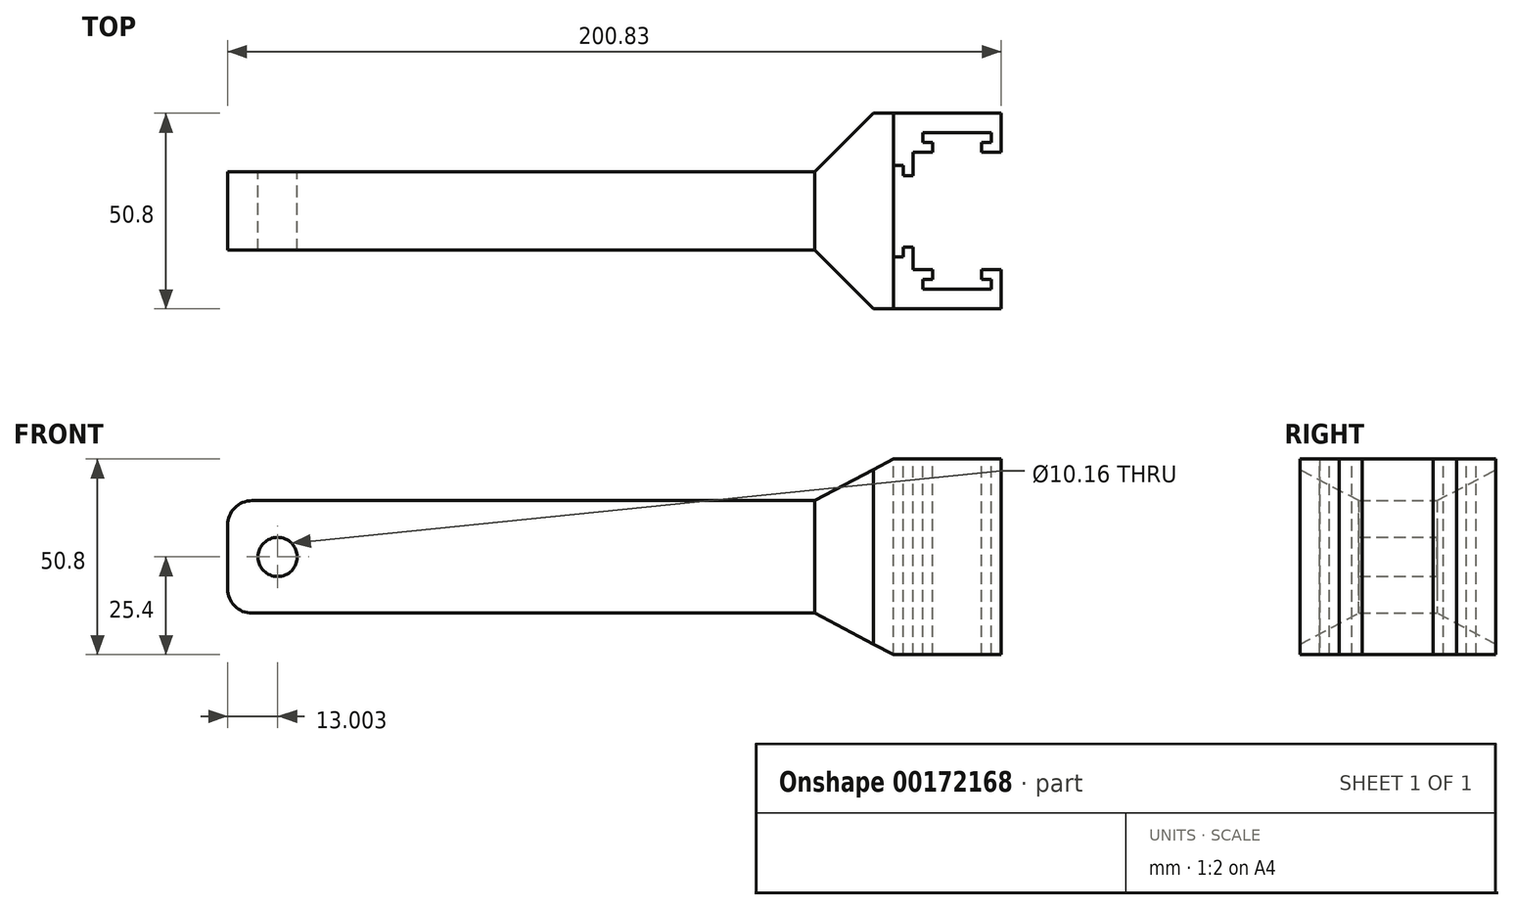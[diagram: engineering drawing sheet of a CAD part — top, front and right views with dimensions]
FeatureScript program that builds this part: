
annotation { "Feature Type Name" : "Feature", "Feature Type Description" : "" }
export const myFeature = defineFeature(function(context is Context, id is Id, definition is map)
    precondition{}
    {
        {
            var Q0;
            Q0=qCreatedBy(makeId("Front.planeOp"),FACE);
            var sketch = newSketch(context, id + "F0", { "sketchPlane" : qUnion([Q0])});
            skLineSegment(sketch, "E0.bottom", {"start": v(76.2, 14.6) * mm, "end": v(-69.85, 14.6) * mm});
            skLineSegment(sketch, "E0.top", {"start": v(76.2, -14.6) * mm, "end": v(-69.85, -14.6) * mm});
            skLineSegment(sketch, "E0.left", {"start": v(76.2, 14.6) * mm, "end": v(76.2, -14.6) * mm});
            skLineSegment(sketch, "E0.right", {"start": v(-76.2, 8.26) * mm, "end": v(-76.2, -8.26) * mm});
            skPoint(sketch, "E0.middle", {"position": v(0, 0) * mm});
            skLineSegment(sketch, "E1.bottom", {"start": v(96.7, 25.4) * mm, "end": v(124.63, 25.4) * mm});
            skLineSegment(sketch, "E1.top", {"start": v(96.7, -25.4) * mm, "end": v(124.63, -25.4) * mm});
            skLineSegment(sketch, "E1.left", {"start": v(96.7, 25.4) * mm, "end": v(96.7, -25.4) * mm});
            skLineSegment(sketch, "E1.right", {"start": v(124.63, 25.4) * mm, "end": v(124.63, -25.4) * mm});
            skPoint(sketch, "E1.middle", {"position": v(110.66, 0) * mm});
            skLineSegment(sketch, "E2", {"start": v(76.2, 14.6) * mm, "end": v(96.7, 25.4) * mm});
            skLineSegment(sketch, "E3", {"start": v(76.2, -14.6) * mm, "end": v(96.7, -25.4) * mm});
            skPoint(sketch, "E4.visualSharp", {"position": v(-76.2, 14.6) * mm});
            skArc(sketch, "E4.filletArc", {"start": v(-69.85, 14.6) * mm, "mid": v(-74.34, 12.75) * mm, "end": v(-76.2, 8.26) * mm});
            skPoint(sketch, "E5.visualSharp", {"position": v(-76.2, -14.6) * mm});
            skArc(sketch, "E5.filletArc", {"start": v(-76.2, -8.26) * mm, "mid": v(-74.34, -12.75) * mm, "end": v(-69.85, -14.6) * mm});
            skCircle(sketch, "E6", {"center": v(-63.2, 0) * mm, "radius": 5.08 * mm});
            skLineSegment(sketch, "E7", {"start": v(101.77, 25.4) * mm, "end": v(101.77, -25.4) * mm});
            skLineSegment(sketch, "E8", {"start": v(119.55, 25.4) * mm, "end": v(119.55, -25.4) * mm});
            skSolve(sketch);
        }
        {
            var Q0;
            Q0=makeQuery(id+"F0.imprint","IMPRINT",FACE,{"disambiguationData":[TD([[makeQuery(id+"F0.imprint","IMPRINT",EDGE,{"derivedFrom":sQuery(id+"F0.wireOp",EDGE,"E0.bottom")}),1.0]])]});
            extrude(context, id + "F1", {"entities" : qUnion([Q0]), "endBound" : BoundingType.SYMMETRIC, "depth" : 20.32 * mm});
        }
        {
            var Q0;
            {var subQ0=sQuery(id+"F0.wireOp",EDGE,"E1.right");Q0=makeQuery(id+"F0.imprint","IMPRINT",FACE,{"disambiguationData":[TD([[makeQuery(id+"F0.imprint","IMPRINT",EDGE,{"derivedFrom":subQ0}),-1.0]])]});}
            var Q1;
            {var subQ0=sQuery(id+"F0.wireOp",EDGE,"E7");Q1=makeQuery(id+"F0.imprint","IMPRINT",FACE,{"disambiguationData":[TD([[makeQuery(id+"F0.imprint","IMPRINT",EDGE,{"derivedFrom":subQ0}),1.0]])]});}
            var Q2;
            {var subQ0=sQuery(id+"F0.wireOp",EDGE,"E1.left");Q2=makeQuery(id+"F0.imprint","IMPRINT",FACE,{"disambiguationData":[TD([[makeQuery(id+"F0.imprint","IMPRINT",EDGE,{"derivedFrom":subQ0}),1.0]])]});}
            var Q3;
            Q3=makeQuery(id+"F0.imprint","IMPRINT",FACE,{"disambiguationData":[TD([[makeQuery(id+"F0.imprint","IMPRINT",EDGE,{"derivedFrom":sQuery(id+"F0.wireOp",EDGE,"E0.left")}),1.0]])]});
            extrude(context, id + "F2", {"entities" : qUnion([Q0, Q1, Q2, Q3]), "endBound" : BoundingType.SYMMETRIC, "depth" : 50.8 * mm});
        }
        {
            var Q0;
            Q0=makeQuery(id+"F2.opExtrude","CAP_EDGE",EDGE,{"disambiguationData":[OSD([sQuery(id+"F0.wireOp",EDGE,"E0.left")])],"isStart":false});
            var Q1;
            Q1=makeQuery(id+"F2.opExtrude","CAP_EDGE",EDGE,{"disambiguationData":[OSD([sQuery(id+"F0.wireOp",EDGE,"E0.left")])],"isStart":true});
            chamfer(context, id + "F3", {"entities" : qUnion([Q0, Q1]), "width" : 15.24 * mm, "tangentPropagation" : true});
        }
        {
            var Q0;
            Q0=makeQuery(id+"F2.opExtrude","SWEPT_FACE",FACE,{"disambiguationData":[OSD([sQuery(id+"F0.wireOp",EDGE,"E1.bottom")])]});
            var sketch = newSketch(context, id + "F4", { "sketchPlane" : qUnion([Q0])});
            skLineSegment(sketch, "E9.bottom", {"start": v(124.63, 12.7) * mm, "end": v(101.77, 12.7) * mm});
            skLineSegment(sketch, "E9.top", {"start": v(124.63, -12.7) * mm, "end": v(101.77, -12.7) * mm});
            skLineSegment(sketch, "E9.left", {"start": v(124.63, 12.7) * mm, "end": v(124.63, -12.7) * mm});
            skLineSegment(sketch, "E9.right", {"start": v(101.77, 12.7) * mm, "end": v(101.77, -12.7) * mm});
            skLineSegment(sketch, "E10.bottom", {"start": v(106.85, -20.32) * mm, "end": v(119.55, -20.32) * mm});
            skLineSegment(sketch, "E10.top", {"start": v(106.85, 20.32) * mm, "end": v(119.55, 20.32) * mm});
            skLineSegment(sketch, "E10.left", {"start": v(106.85, -20.32) * mm, "end": v(106.85, 20.32) * mm});
            skLineSegment(sketch, "E10.right", {"start": v(119.55, -20.32) * mm, "end": v(119.55, 20.32) * mm});
            skPoint(sketch, "E10.middle", {"position": v(113.2, 0) * mm});
            skLineSegment(sketch, "E11.bottom", {"start": v(101.77, -15.24) * mm, "end": v(147.5, -15.24) * mm});
            skLineSegment(sketch, "E11.top", {"start": v(101.77, 15.24) * mm, "end": v(147.5, 15.24) * mm});
            skLineSegment(sketch, "E11.left", {"start": v(101.77, -15.24) * mm, "end": v(101.77, 15.24) * mm});
            skLineSegment(sketch, "E11.right", {"start": v(147.5, -15.24) * mm, "end": v(147.5, 15.24) * mm});
            skPoint(sketch, "E11.middle", {"position": v(124.63, 0) * mm});
            skSolve(sketch);
        }
        {
            var Q0;
            Q0=makeQuery(id+"F4.imprint","IMPRINT",FACE,{"disambiguationData":[TD([[makeQuery(id+"F4.imprint","IMPRINT",EDGE,{"derivedFrom":sQuery(id+"F4.wireOp",EDGE,"E9.bottom")}),1.0]])]});
            extrude(context, id + "F5", {"entities" : qUnion([Q0]), "operationType" : NewBodyOperationType.REMOVE, "oppositeDirection" : true, "depth" : 64.77 * mm});
        }
        {
            var Q0;
            {var subQ0=sQuery(id+"F4.wireOp",EDGE,"E10.right");var subQ1=sQuery(id+"F4.wireOp",EDGE,"E9.bottom");var subQ2=makeQuery(id+"F4.imprint","INTERSECT",VERTEX,{"derivedFrom":[subQ1,subQ0]});Q0=makeQuery(id+"F4.imprint","IMPRINT",FACE,{"disambiguationData":[TD([[makeQuery(id+"F4.imprint","IMPRINT",EDGE,{"disambiguationData":[TD([[subQ2,-1.0]])],"derivedFrom":subQ1}),-1.0]])]});}
            var Q1;
            {var subQ0=sQuery(id+"F4.wireOp",EDGE,"E10.top");Q1=makeQuery(id+"F4.imprint","IMPRINT",FACE,{"disambiguationData":[TD([[makeQuery(id+"F4.imprint","IMPRINT",EDGE,{"derivedFrom":subQ0}),-1.0]])]});}
            var Q2;
            {var subQ0=sQuery(id+"F4.wireOp",EDGE,"E10.right");var subQ1=sQuery(id+"F4.wireOp",EDGE,"E9.top");var subQ2=makeQuery(id+"F4.imprint","INTERSECT",VERTEX,{"derivedFrom":[subQ1,subQ0]});Q2=makeQuery(id+"F4.imprint","IMPRINT",FACE,{"disambiguationData":[TD([[makeQuery(id+"F4.imprint","IMPRINT",EDGE,{"disambiguationData":[TD([[subQ2,-1.0]])],"derivedFrom":subQ1}),1.0]])]});}
            var Q3;
            {var subQ0=sQuery(id+"F4.wireOp",EDGE,"E10.bottom");Q3=makeQuery(id+"F4.imprint","IMPRINT",FACE,{"disambiguationData":[TD([[makeQuery(id+"F4.imprint","IMPRINT",EDGE,{"derivedFrom":subQ0}),1.0]])]});}
            var Q4;
            {var subQ0=sQuery(id+"F4.wireOp",EDGE,"E11.left");var subQ1=sQuery(id+"F4.wireOp",EDGE,"E9.bottom");var subQ2=makeQuery(id+"F4.imprint","INTERSECT",VERTEX,{"derivedFrom":[subQ1,subQ0]});Q4=makeQuery(id+"F4.imprint","IMPRINT",FACE,{"disambiguationData":[TD([[makeQuery(id+"F4.imprint","IMPRINT",EDGE,{"disambiguationData":[TD([[subQ2,1.0]])],"derivedFrom":subQ1}),-1.0]])]});}
            var Q5;
            {var subQ0=sQuery(id+"F4.wireOp",EDGE,"E9.bottom");var subQ3=sQuery(id+"F4.wireOp",EDGE,"E10.right");var subQ4=makeQuery(id+"F4.imprint","INTERSECT",VERTEX,{"derivedFrom":[subQ0,subQ3]});Q5=makeQuery(id+"F4.imprint","IMPRINT",FACE,{"disambiguationData":[TD([[makeQuery(id+"F4.imprint","IMPRINT",EDGE,{"disambiguationData":[TD([[subQ4,-1.0]])],"derivedFrom":subQ3}),-1.0]])]});}
            var Q6;
            {var subQ0=sQuery(id+"F4.wireOp",EDGE,"E9.top");var subQ3=sQuery(id+"F4.wireOp",EDGE,"E10.right");var subQ4=makeQuery(id+"F4.imprint","INTERSECT",VERTEX,{"derivedFrom":[subQ0,subQ3]});Q6=makeQuery(id+"F4.imprint","IMPRINT",FACE,{"disambiguationData":[TD([[makeQuery(id+"F4.imprint","IMPRINT",EDGE,{"disambiguationData":[TD([[subQ4,1.0]])],"derivedFrom":subQ3}),-1.0]])]});}
            var Q7;
            {var subQ0=sQuery(id+"F4.wireOp",EDGE,"E11.left");var subQ1=sQuery(id+"F4.wireOp",EDGE,"E9.top");var subQ2=makeQuery(id+"F4.imprint","INTERSECT",VERTEX,{"derivedFrom":[subQ1,subQ0]});Q7=makeQuery(id+"F4.imprint","IMPRINT",FACE,{"disambiguationData":[TD([[makeQuery(id+"F4.imprint","IMPRINT",EDGE,{"disambiguationData":[TD([[subQ2,1.0]])],"derivedFrom":subQ1}),1.0]])]});}
            extrude(context, id + "F6", {"entities" : qUnion([Q0, Q1, Q2, Q3, Q4, Q5, Q6, Q7]), "operationType" : NewBodyOperationType.REMOVE, "endBound" : BoundingType.SYMMETRIC, "oppositeDirection" : true, "depth" : 159 * mm});
        }
        {
            var Q0;
            {var subQ15=sQuery(id+"F4.wireOp",EDGE,"E10.bottom");Q0=makeQuery(id+"F4.imprint","IMPRINT",FACE,{"disambiguationData":[TD([[makeQuery(id+"F4.imprint","IMPRINT",EDGE,{"derivedFrom":subQ15}),-1.0]])]});}
            var sketch = newSketch(context, id + "F7", { "sketchPlane" : qUnion([Q0])});
            skLineSegment(sketch, "E12.bottom", {"start": v(122.1, 20.33) * mm, "end": v(104.31, 20.33) * mm});
            skLineSegment(sketch, "E12.top", {"start": v(122.1, 17.78) * mm, "end": v(104.31, 17.78) * mm});
            skLineSegment(sketch, "E12.left", {"start": v(122.1, 20.33) * mm, "end": v(122.1, 17.78) * mm});
            skLineSegment(sketch, "E12.right", {"start": v(104.31, 20.33) * mm, "end": v(104.31, 17.78) * mm});
            skLineSegment(sketch, "E13.bottom", {"start": v(104.31, 17.78) * mm, "end": v(122.1, 17.78) * mm, "construction": true});
            skLineSegment(sketch, "E13.top", {"start": v(104.31, -17.78) * mm, "end": v(122.1, -17.78) * mm, "construction": true});
            skLineSegment(sketch, "E13.left", {"start": v(104.31, 17.78) * mm, "end": v(104.31, -17.78) * mm, "construction": true});
            skLineSegment(sketch, "E13.right", {"start": v(122.1, 17.78) * mm, "end": v(122.1, -17.78) * mm, "construction": true});
            skLineSegment(sketch, "E14.bottom", {"start": v(104.31, -17.78) * mm, "end": v(122.1, -17.78) * mm});
            skLineSegment(sketch, "E14.top", {"start": v(104.31, -20.31) * mm, "end": v(122.1, -20.31) * mm});
            skLineSegment(sketch, "E14.left", {"start": v(104.31, -17.78) * mm, "end": v(104.31, -20.31) * mm});
            skLineSegment(sketch, "E14.right", {"start": v(122.1, -17.78) * mm, "end": v(122.1, -20.31) * mm});
            skSolve(sketch);
        }
        {
            var Q0;
            Q0=makeQuery(id+"F7.imprint","IMPRINT",FACE,{"disambiguationData":[TD([[makeQuery(id+"F7.imprint","IMPRINT",EDGE,{"derivedFrom":sQuery(id+"F7.wireOp",EDGE,"E12.bottom")}),1.0]])]});
            extrude(context, id + "F8", {"entities" : qUnion([Q0]), "operationType" : NewBodyOperationType.REMOVE, "oppositeDirection" : true, "depth" : 59.44 * mm});
        }
        {
            var Q0;
            {var subQ0=sQuery(id+"F7.wireOp",EDGE,"E14.left");Q0=makeQuery(id+"F7.imprint","IMPRINT",FACE,{"disambiguationData":[TD([[makeQuery(id+"F7.imprint","IMPRINT",EDGE,{"derivedFrom":subQ0}),1.0]])]});}
            var Q1;
            {var subQ0=sQuery(id+"F7.wireOp",EDGE,"E14.right");Q1=makeQuery(id+"F7.imprint","IMPRINT",FACE,{"disambiguationData":[TD([[makeQuery(id+"F7.imprint","IMPRINT",EDGE,{"derivedFrom":subQ0}),-1.0]])]});}
            extrude(context, id + "F9", {"entities" : qUnion([Q0, Q1]), "operationType" : NewBodyOperationType.REMOVE, "oppositeDirection" : true, "depth" : 72.9 * mm});
        }
        {
            var Q0;
            {var subQ15=sQuery(id+"F4.wireOp",EDGE,"E10.bottom");Q0=makeQuery(id+"F4.imprint","IMPRINT",FACE,{"disambiguationData":[TD([[makeQuery(id+"F4.imprint","IMPRINT",EDGE,{"derivedFrom":subQ15}),-1.0]])]});}
            var sketch = newSketch(context, id + "F10", { "sketchPlane" : qUnion([Q0])});
            skLineSegment(sketch, "E15.bottom", {"start": v(101.77, 11.8) * mm, "end": v(96.7, 11.8) * mm});
            skLineSegment(sketch, "E15.top", {"start": v(101.77, -11.94) * mm, "end": v(96.7, -11.94) * mm});
            skLineSegment(sketch, "E15.left", {"start": v(101.77, 11.8) * mm, "end": v(101.77, -11.94) * mm});
            skLineSegment(sketch, "E15.right", {"start": v(96.7, 11.8) * mm, "end": v(96.7, -11.94) * mm});
            skLineSegment(sketch, "E16.bottom", {"start": v(101.77, 11.8) * mm, "end": v(99.23, 11.8) * mm});
            skLineSegment(sketch, "E16.top", {"start": v(101.77, -11.94) * mm, "end": v(99.23, -11.94) * mm});
            skLineSegment(sketch, "E16.right", {"start": v(99.23, 11.8) * mm, "end": v(99.23, -11.94) * mm});
            skLineSegment(sketch, "E17", {"start": v(101.77, -9.3) * mm, "end": v(99.23, -9.3) * mm});
            skLineSegment(sketch, "E18", {"start": v(101.77, 9.17) * mm, "end": v(99.23, 9.17) * mm});
            skSolve(sketch);
        }
        {
            var Q0;
            {var subQ0=sQuery(id+"F10.wireOp",EDGE,"E17");Q0=makeQuery(id+"F10.imprint","IMPRINT",FACE,{"disambiguationData":[TD([[makeQuery(id+"F10.imprint","IMPRINT",EDGE,{"derivedFrom":subQ0}),-1.0]])]});}
            var Q1;
            {var subQ0=sQuery(id+"F10.wireOp",EDGE,"E16.right");var subQ1=makeQuery(id+"F10.imprint","INTERSECT",VERTEX,{"derivedFrom":[subQ0,sQuery(id+"F10.wireOp",EDGE,"E17")]});Q1=makeQuery(id+"F10.imprint","IMPRINT",FACE,{"disambiguationData":[TD([[makeQuery(id+"F10.imprint","IMPRINT",EDGE,{"disambiguationData":[TD([[subQ1,1.0]])],"derivedFrom":subQ0}),-1.0]])]});}
            extrude(context, id + "F11", {"entities" : qUnion([Q0, Q1]), "operationType" : NewBodyOperationType.REMOVE, "oppositeDirection" : true, "depth" : 76.2 * mm});
        }
    });
